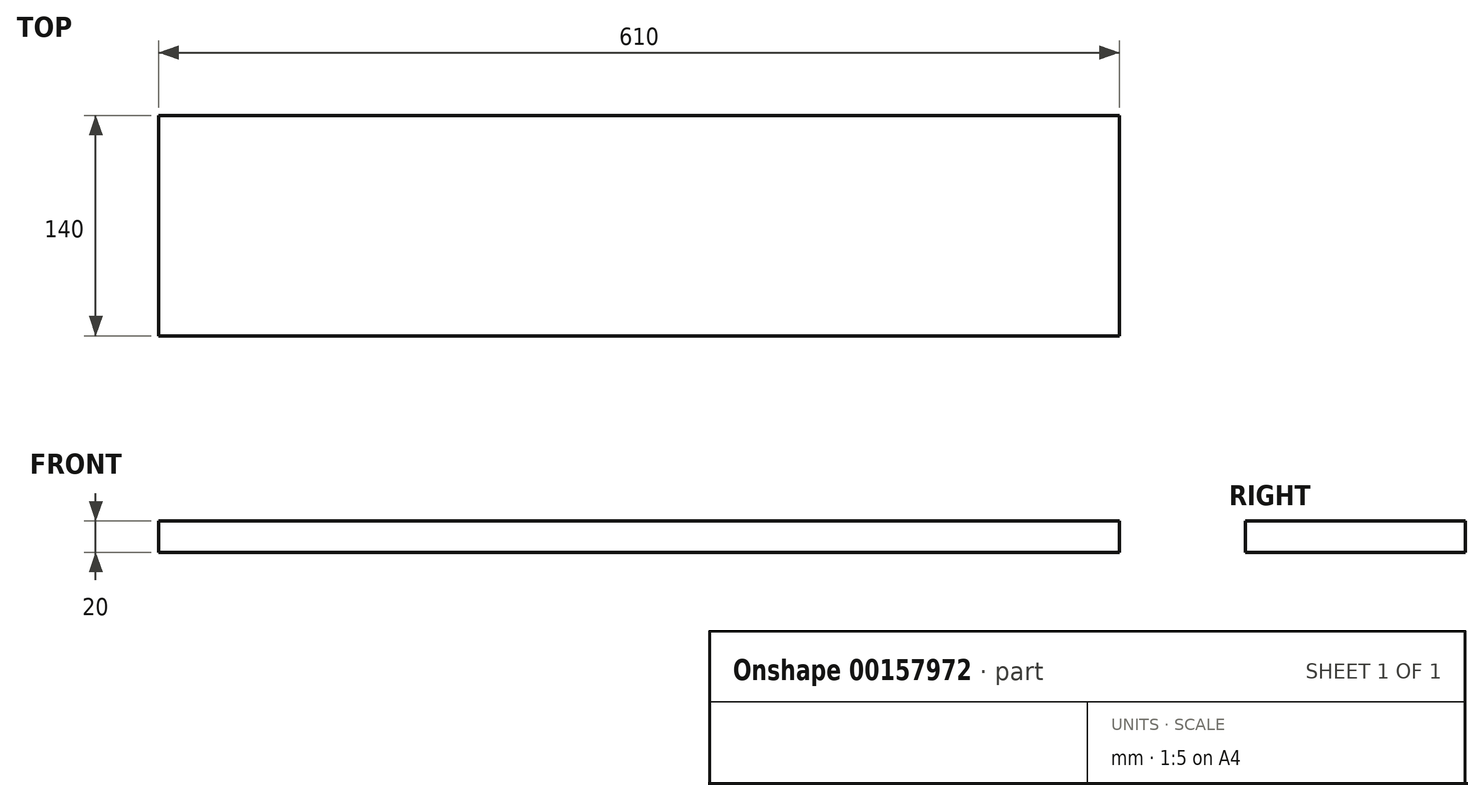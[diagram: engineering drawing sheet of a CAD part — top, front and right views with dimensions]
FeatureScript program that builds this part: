
annotation { "Feature Type Name" : "Feature", "Feature Type Description" : "" }
export const myFeature = defineFeature(function(context is Context, id is Id, definition is map)
    precondition{}
    {
        {
            var Q0;
            Q0=qCreatedBy(makeId("Top.planeOp"),FACE);
            var sketch = newSketch(context, id + "F0", { "sketchPlane" : qUnion([Q0])});
            skLineSegment(sketch, "E0.bottom", {"start": v(-305, -70) * mm, "end": v(305, -70) * mm});
            skLineSegment(sketch, "E0.top", {"start": v(-305, 70) * mm, "end": v(305, 70) * mm});
            skLineSegment(sketch, "E0.left", {"start": v(-305, -70) * mm, "end": v(-305, 70) * mm});
            skLineSegment(sketch, "E0.right", {"start": v(305, -70) * mm, "end": v(305, 70) * mm});
            skPoint(sketch, "E0.middle", {"position": v(0, 0) * mm});
            skSolve(sketch);
        }
        {
            var Q0;
            Q0 = qSketchRegion(id + "F0", true);
            extrude(context, id + "F1", {"entities" : qUnion([Q0]), "endBound" : BoundingType.SYMMETRIC, "depth" : 20 * mm});
        }
    });
